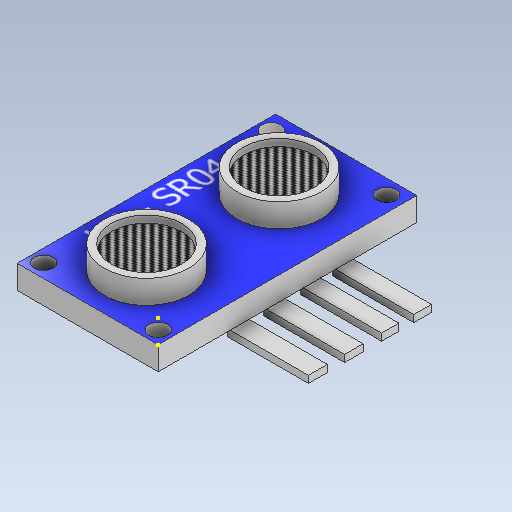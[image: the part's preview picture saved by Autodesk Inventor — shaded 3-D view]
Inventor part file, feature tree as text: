
AUTODESK INVENTOR PART (.ipt)
format: ipt  version: 2021 (Build 250183000, 183)  size: 214,528 bytes
history: native  units: mm
features: sketch x8, extrude x3, hole x3
ambient origin geometry x8: Origin, YZ Plane, XZ Plane, XY Plane, X Axis, Y Axis, Z Axis, Center Point
bodies: Solid1 (feature_tree)
feature tree (14):
  sketch  "Sketch1"  dims[d0=110.0mm d1=60.0mm]
  sketch  "Sketch2"  dims[d2=10.0mm d3=0.0mm d4=3.0mm d5=0.0mm]
  extrude  "Extrusion1"  Depth=60.0mm
  extrude  "Extrusion2"  Depth=3.0mm TaperAngle=0.0deg
  extrude  "Extrusion3"  [1 undecoded]
  sketch  "Sketch4"  dims[d8=30.0mm d9=6.0mm d10=4.0mm d11=2.0mm d12=90.0deg d13=3.0mm d14=0.0mm]
  hole  "Hole1"  [1 undecoded]
  hole  "Hole2"  [1 undecoded]
  hole  "Hole3"  [1 undecoded]
  sketch  "Sketch8"
  sketch  "Sketch3"  dims[d6=10.0mm d7=0.0mm]
  sketch  "Sketch5"  dims[d15=30.0mm d16=6.0mm d17=4.0mm d18=2.0mm d19=90.0deg d20=3.0mm d21=0.0mm]
  sketch  "Sketch6"  dims[d22=8.0mm d23=6.0mm d24=4.0mm d25=2.0mm d26=90.0deg d27=3.0mm d28=0.0mm]
  sketch  "Sketch7"
note: 4 required parameter values undecoded (feature->parameter linkage not recoverable at this tier; creation-order binding heuristic only, values carry confidence <= 0.55)
